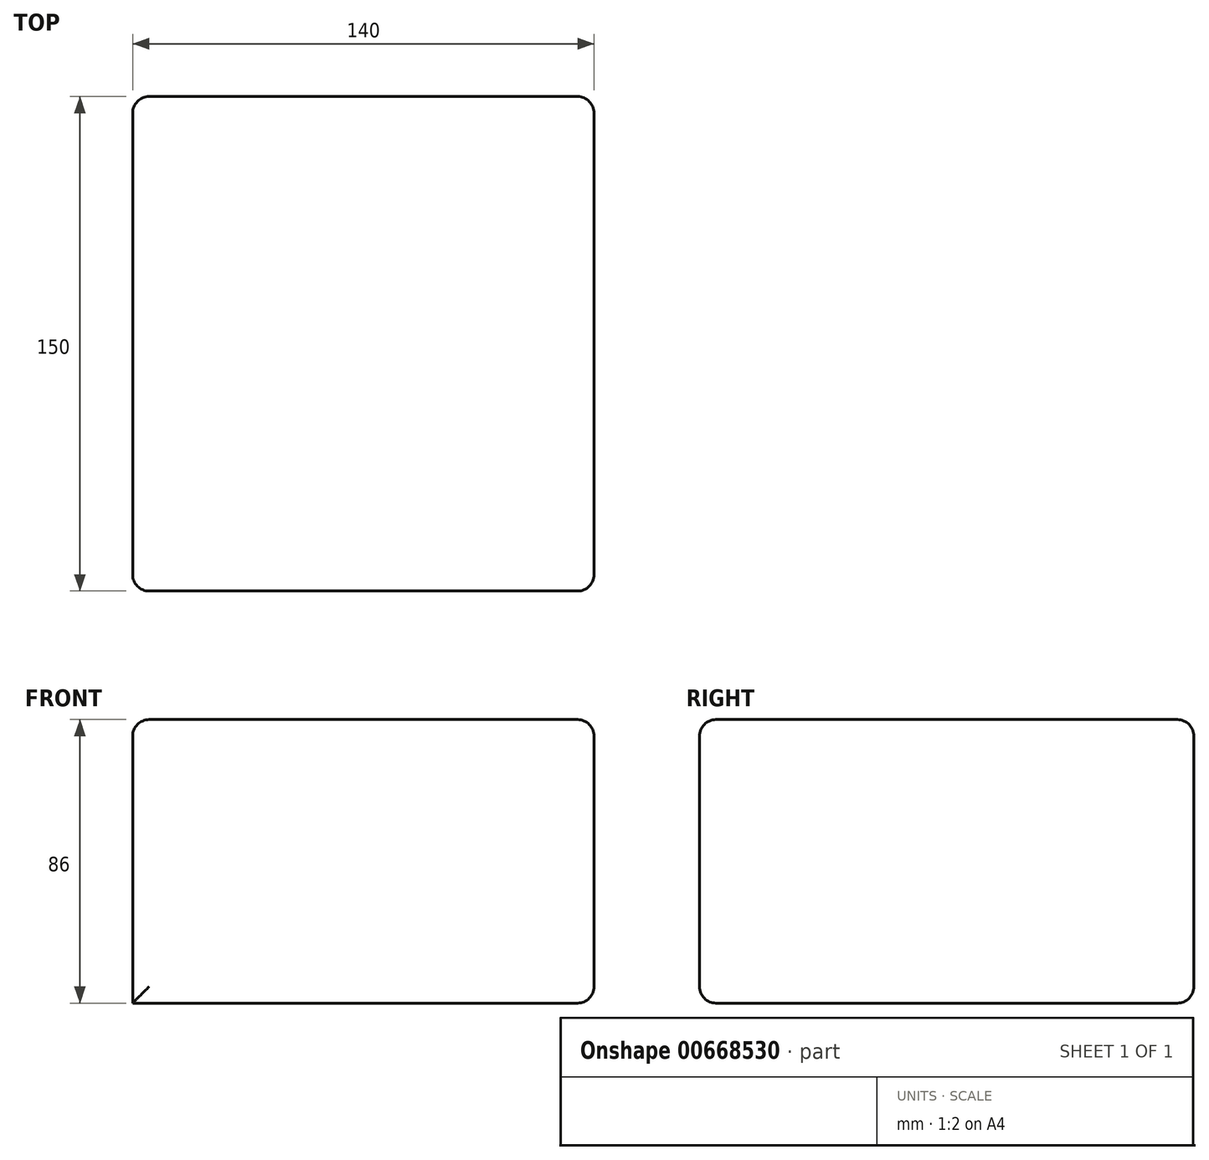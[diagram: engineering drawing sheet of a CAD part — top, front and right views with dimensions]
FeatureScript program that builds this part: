
annotation { "Feature Type Name" : "Feature", "Feature Type Description" : "" }
export const myFeature = defineFeature(function(context is Context, id is Id, definition is map)
    precondition{}
    {
        {
            var Q0;
            Q0=qCreatedBy(makeId("Top.planeOp"),FACE);
            var sketch = newSketch(context, id + "F0", { "sketchPlane" : qUnion([Q0])});
            skLineSegment(sketch, "E0.bottom", {"start": v(70, 75) * mm, "end": v(-70, 75) * mm});
            skLineSegment(sketch, "E0.top", {"start": v(70, -75) * mm, "end": v(-70, -75) * mm});
            skLineSegment(sketch, "E0.left", {"start": v(70, 75) * mm, "end": v(70, -75) * mm});
            skLineSegment(sketch, "E0.right", {"start": v(-70, 75) * mm, "end": v(-70, -75) * mm});
            skPoint(sketch, "E0.middle", {"position": v(0, 0) * mm});
            skSolve(sketch);
        }
        {
            var Q0;
            Q0=makeQuery(id+"F0.imprint","IMPRINT",FACE,{"disambiguationData":[TD([[makeQuery(id+"F0.imprint","IMPRINT",EDGE,{"derivedFrom":sQuery(id+"F0.wireOp",EDGE,"E0.bottom")}),1.0]])]});
            extrude(context, id + "F1", {"entities" : qUnion([Q0]), "depth" : 86 * mm, "offsetDistance" : 25 * mm});
        }
        {
            var Q0;
            Q0=makeQuery(id+"F1.opExtrude","SWEPT_FACE",FACE,{"disambiguationData":[OSD([sQuery(id+"F0.wireOp",EDGE,"E0.top")])]});
            var Q1;
            Q1=makeQuery(id+"F1.opExtrude","SWEPT_FACE",FACE,{"disambiguationData":[OSD([sQuery(id+"F0.wireOp",EDGE,"E0.left")])]});
            var Q2;
            Q2=makeQuery(id+"F1.opExtrude","SWEPT_FACE",FACE,{"disambiguationData":[OSD([sQuery(id+"F0.wireOp",EDGE,"E0.bottom")])]});
            var Q3;
            Q3=makeQuery(id+"F1.opExtrude","CAP_FACE",FACE,{"disambiguationData":[OSD([sQuery(id+"F0.wireOp",EDGE,"E0.bottom"),sQuery(id+"F0.wireOp",EDGE,"E0.top"),sQuery(id+"F0.wireOp",EDGE,"E0.left"),sQuery(id+"F0.wireOp",EDGE,"E0.right")])],"isStart":false});
            fillet(context, id + "F2", {"entities" : qUnion([Q0, Q1, Q2, Q3]), "radius" : 5 * mm, "tangentPropagation" : true, "allowEdgeOverflow" : false});
        }
    });
